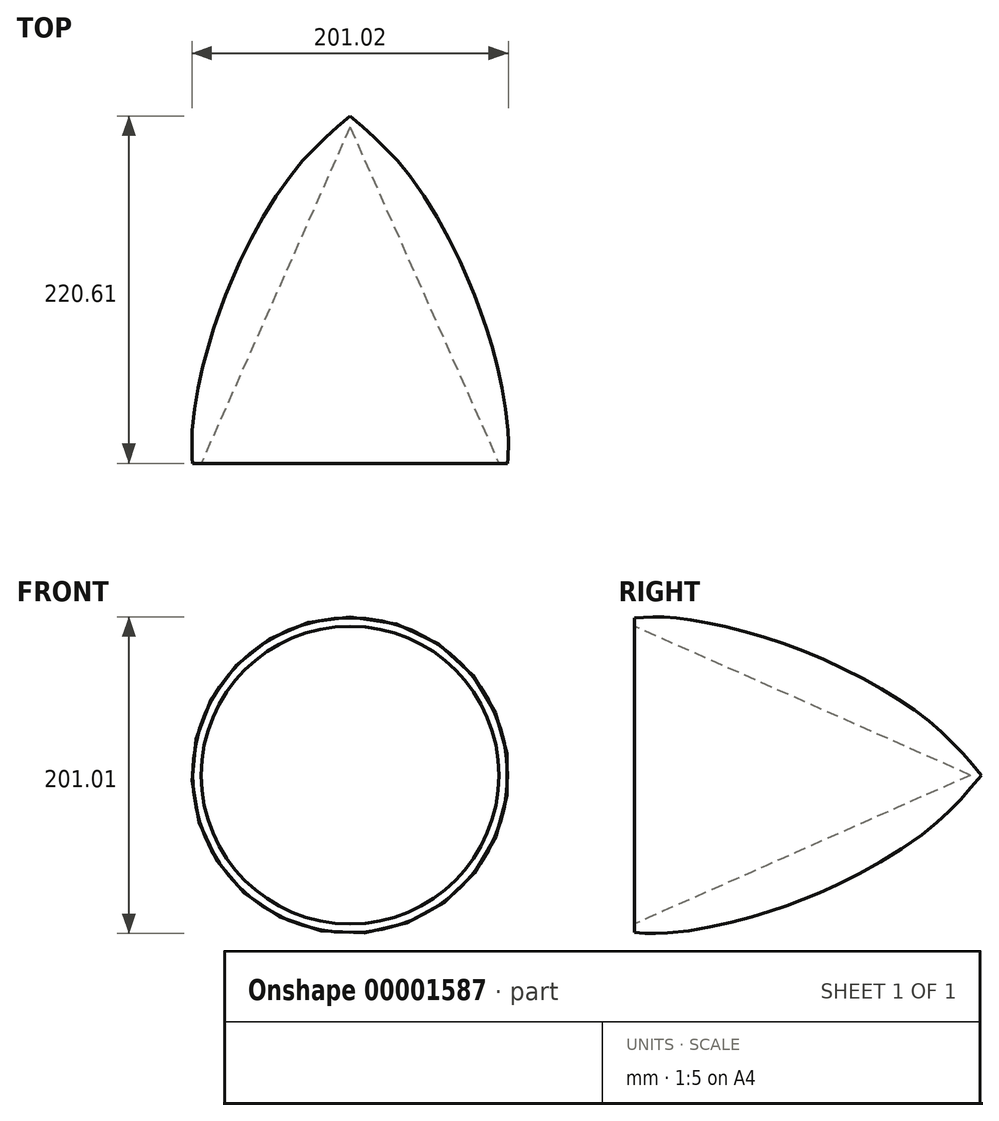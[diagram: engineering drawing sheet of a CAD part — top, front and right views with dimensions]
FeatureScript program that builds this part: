
annotation { "Feature Type Name" : "Feature", "Feature Type Description" : "" }
export const myFeature = defineFeature(function(context is Context, id is Id, definition is map)
    precondition{}
    {
        {
            var Q0;
            Q0=qCreatedBy(makeId("Right.planeOp"),FACE);
            var sketch = newSketch(context, id + "F0", { "sketchPlane" : qUnion([Q0])});
            skLineSegment(sketch, "E0", {"start": v(0, 0) * mm, "end": v(0, 100) * mm, "construction": true});
            skFitSpline(sketch, "E1", {"points": [v(0, 100) * mm, v(24.24, 100) * mm, v(96.36, 83.03) * mm, v(183.03, 37.58) * mm, v(220.6, 0) * mm], "startDerivative": vector(132.4, 8.2) * mm, "endDerivative": vector(134.16, -158.2) * mm});
            skLineSegment(sketch, "E2", {"start": v(220.6, 0) * mm, "end": v(0, 0) * mm, "construction": true});
            skLineSegment(sketch, "E3", {"start": v(0, 100) * mm, "end": v(0, 94.57) * mm});
            skLineSegment(sketch, "E4", {"start": v(0, 94.57) * mm, "end": v(213.6, 0) * mm});
            skLineSegment(sketch, "E5", {"start": v(213.6, 0) * mm, "end": v(220.6, 0) * mm});
            skSolve(sketch);
        }
        {
            var Q0;
            Q0=makeQuery(id+"F0.imprint","IMPRINT",FACE,{"disambiguationData":[TD([[makeQuery(id+"F0.imprint","IMPRINT",EDGE,{"derivedFrom":sQuery(id+"F0.wireOp",EDGE,"E1")}),-1.0]])]});
            var Q1;
            Q1=sQuery(id+"F0.wireOp",EDGE,"E1");
            var Q2;
            Q2=sQuery(id+"F0.wireOp",EDGE,"E0");
            var Q3;
            Q3=sQuery(id+"F0.wireOp",EDGE,"E2");
            revolve(context, id + "F1", {"entities" : qUnion([Q0]), "surfaceEntities" : qUnion([Q1, Q2]), "axis" : qUnion([Q3]), "revolveType" : RevolveType.FULL});
        }
    });
